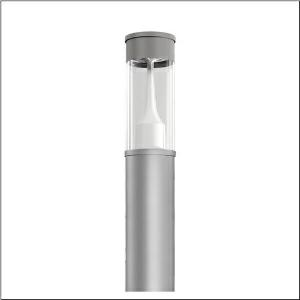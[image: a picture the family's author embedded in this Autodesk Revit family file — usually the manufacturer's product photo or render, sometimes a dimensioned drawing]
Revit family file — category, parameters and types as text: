
# Revit family: city-light_400_iq___p1_0a_5xa5305ff14hp_6c14
name_source: partatom
category: Lighting Fixtures
units: mm (PartAtom-declared; Revit-internal decimal feet)

## family parameters
Cut with Voids When Loaded = No
Host = Face
Light Source = No
Part Type = Normal
Room Calculation Point = No
Round Connector Dimension = Use Diameter
Shared = No

## types (1)
- --- (1 x LED, 4700 lm, 33.6 W, 3000K)
    Apparent Load = 34 VA
    CIE Flux Codes = 31 62 91 95 100
    Color Rendering = 70
    Color Temperature = 3000K
    Default Elevation = 1800 mm
    Description = City-Light 400 iQ, light pillar, Module 540 iQ-SR, primary light control with 3 zone facetted reflector, of plastic, silver coated, highly specular, structured, primary optical cover: cover, of PMMA, transparent, partly coated, light distribution: P1.0a, primary light characteristic: strongly asymmetric, LED, High Power LED, rated luminous flux: 4.700lm, luminous efficacy: 140lm/W, light colour: 730, colour temperature: 3000K, control gear: ECG iQ, control: presetting dimming logarithmic, Street-Remote, Auto-Match, Temp-Guard, Lumen-Switch, Night-Set, Smart-Wire, Light-Fading, Desk-Remote (wireless, voltage-free reading and setting of iQ features in the workshop via application-optimized NFC function/RFID function), optimised constant luminous flux control (CLO 2.0), with terminal, 6-pole, max. 2.5mm², mains connection: 230..240V, AC, 50/60Hz, start of lifetime: 34W, end of service life: 36W, reduction: 15W, luminaire housing, cylindrical, of extruded aluminium section, coated, Siteco® metallic grey (DB 702S), length: 4.694mm, diameter: 200mm, Module 540 iQ-SR, traffic white (RAL 9016), equipment: Power, protection rating (complete): IP65, insulation class (complete): insulation class II (safety insulation), certification: CE, ENEC, VDE, packaging unit: 1 piece

Light Distribution: P1.0a
    Height = 500 mm
    Lamp = 1 x LED
    Lamp Light Flux = 4700 lm
    Lamp Power = 33.6 W
    Lamp count = 1
    Length = 200 mm  [stored 0.656168 ft]
    Luminous efficacy = 140 lm/W
    Manufacturer = Siteco
    ModVariant = No
    Model = 5XA5305FF14HP
    Mounting Place = Floor
    Mounting Type = Freestanding
    Number of Poles = 1
    OnlyDefault = Yes
    Power Factor = 1
    Product Name = City-Light 400 iQ | P1.0a
    Product group = light pillar
    ProductGroupID = 1303
    Protection Class = Protection class II
    Protection Degree = IP 65
    RLX_Detail_Level = 1
    RLX_Emergency_Light_Flux = 0 lm
    RLX_Emergency_Type = 0
    RLX_Emergency_Type_DB = No
    RlxData = <blob elided: 53569 chars, md5=28757857>
    Socket = socket
    Standby Power = 0 W
    System Light Flux = 4700 lm
    System Power = 34 W
    Type Comments = factory setting: luminous flux: 100 % | dim-lin: 254 | 695 mA
    Type Image = l_1006916.jpg
    URL = http://relux.com
    VarID = @adj_145391
    Voltage = 0 V
    Weight = 0.00 kg
    Width = 0 mm  [stored 0 ft]

note: [stored X ft] marks values corroborated as IEEE doubles in the binary element streams (Revit-internal decimal feet)

## geometry (parser evidence)
native form markers: Blend x4, Sweep x13
no freeform markers — native parametric forms only
